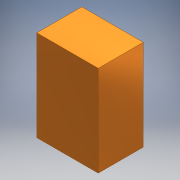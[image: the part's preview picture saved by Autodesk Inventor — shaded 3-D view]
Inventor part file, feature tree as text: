
AUTODESK INVENTOR PART (.ipt)
format: ipt  version: 2016 (Build 200138000, 138)  size: 86,528 bytes
history: native  units: mm
features: extrude x1, sketch x1
ambient origin geometry x8: Origin, YZ Plane, XZ Plane, XY Plane, X Axis, Y Axis, Z Axis, Center Point
bodies: Solid1 (feature_tree)
feature tree (2):
  extrude  "Extrusion1"  Depth=5.2mm
  sketch  "Sketch1"  dims[d0=7.1mm d1=5.2mm d2=10.5mm d3=0.0mm]
